FCSTD DOCUMENT  (FreeCAD 0.21R33771 (Git))
Label: rpi_case_JB_070624
License: All rights reserved
LicenseURL: http://en.wikipedia.org/wiki/All_rights_reserved
objects: Sketcher::SketchObject×2, PartDesign::Plane×1, PartDesign::Body×1
note: 4 computed .brp shape members not serialized (recipe doc carries the construction recipe); baked Part::Feature solids carry a one-line shape summary decoded from their .brp

FEATURE [PartDesign::Plane] DatumPlane
  AttachmentOffset = pos=(-2,0,0) rot=(1,0,0;0.785398rad)
  Length = 66.8033
  MapMode = 2
  Placement = pos=(-2,0,0) rot=(1,0,0;0.785398rad)
  ResizeMode = 0
  Support = -> [XY_Plane]
  Width = 120.159
FEATURE [Sketcher::SketchObject] Sketch001  label="Wall_Outline"
  FullyConstrained = true
  MapMode = 5
  Placement = pos=(-2,0,0) rot=(1,0,0;0.785398rad)
  Support = -> [DatumPlane]
  sketch-geometry (10):
    g0: LineSegment StartX=-25 StartY=70 StartZ=0 EndX=-25 EndY=0 EndZ=0
    g1: LineSegment StartX=-25 StartY=0 StartZ=0 EndX=25 EndY=0 EndZ=0
    g2: LineSegment StartX=25 StartY=0 StartZ=0 EndX=25 EndY=70 EndZ=0
    g3: LineSegment StartX=25 StartY=70 StartZ=0 EndX=-25 EndY=70 EndZ=0
    g4: GeomPoint X=0 Y=35 Z=0
    g5: LineSegment StartX=20 StartY=5 StartZ=0 EndX=20 EndY=65 EndZ=0
    g6: LineSegment StartX=20 StartY=65 StartZ=0 EndX=-20 EndY=65 EndZ=0
    g7: LineSegment StartX=-20 StartY=65 StartZ=0 EndX=-20 EndY=5 EndZ=0
    g8: LineSegment StartX=-20 StartY=5 StartZ=0 EndX=20 EndY=5 EndZ=0
    g9: GeomPoint X=0 Y=35 Z=0
  constraints (26):
    c: Coincident(g0,g1)
    c: Coincident(g1,g2)
    c: Coincident(g2,g3)
    c: Coincident(g3,g0)
    c: Horizontal(g1)
    c: Horizontal(g3)
    c: Vertical(g0)
    c: Vertical(g2)
    c: Symmetric(g1,g0,g4)
    c: PointOnObject(g4,g-2)
    c: PointOnObject(g-1,g1)
    c: Coincident(g5,g6)
    c: Coincident(g6,g7)
    c: Coincident(g7,g8)
    c: Coincident(g8,g5)
    c: Horizontal(g6)
    c: Horizontal(g8)
    c: Vertical(g5)
    c: Vertical(g7)
    c: Symmetric(g6,g5,g9)
    c: PointOnObject(g9,g-2)
    c: DistanceY(g1,g5) = 5
    c: DistanceY(g5,g2) = 5
    c: DistanceX(g5,g2) = 5
    c: DistanceX(g6,g6) = 40
    c: DistanceY(g7,g7) = 60
FEATURE [Sketcher::SketchObject] Sketch  label="Side_Profile_Outline"
  FullyConstrained = true
  MapMode = 5
  Placement = pos=(0,0,0) rot=(0.57735,0.57735,0.57735;2.0944rad)
  Support = -> [YZ_Plane]
  sketch-geometry (4):
    g0: LineSegment StartX=0 StartY=0 StartZ=0 EndX=56.5685 EndY=56.5685 EndZ=0
    g1: LineSegment StartX=0 StartY=0 StartZ=0 EndX=-14.1421 EndY=14.1421 EndZ=0
    g2: LineSegment StartX=-14.1421 StartY=14.1421 StartZ=0 EndX=42.4264 EndY=70.7107 EndZ=0
    g3: LineSegment StartX=56.5685 StartY=56.5685 StartZ=0 EndX=42.4264 EndY=70.7107 EndZ=0
  constraints (11):
    c: Coincident(g0,g-1)
    c: Angle(g-1,g0) = 0.785398
    c: Coincident(g1,g0)
    c: Coincident(g2,g1)
    c: Coincident(g3,g0)
    c: Coincident(g2,g3)
    c: Parallel(g3,g1)
    c: Parallel(g2,g0)
    c: Angle(g0,g1) = 1.5708
    c: Distance(g3) = 20
    c: Distance(g0) = 80
FEATURE [PartDesign::Body] Body
  Group = -> [DatumPlane,Sketch001,Sketch]
  Origin = -> Origin
